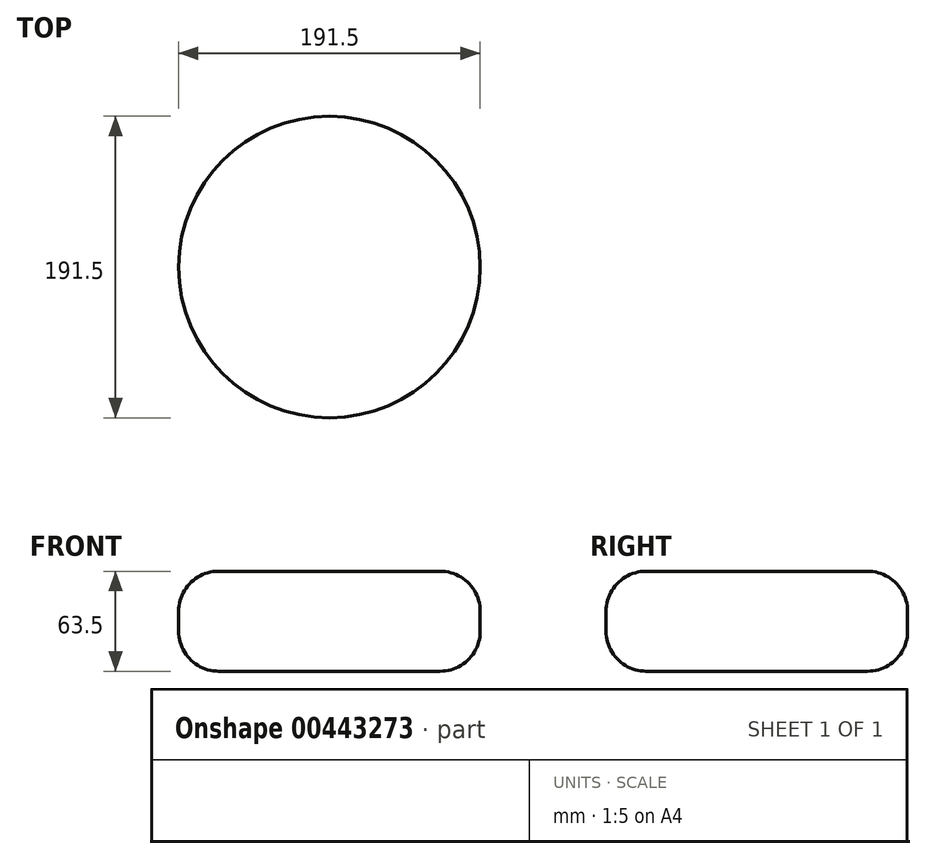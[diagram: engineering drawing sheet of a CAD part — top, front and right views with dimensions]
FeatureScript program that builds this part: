
annotation { "Feature Type Name" : "Feature", "Feature Type Description" : "" }
export const myFeature = defineFeature(function(context is Context, id is Id, definition is map)
    precondition{}
    {
        {
            var Q0;
            Q0=qCreatedBy(makeId("Top.planeOp"),FACE);
            var sketch = newSketch(context, id + "F0", { "sketchPlane" : qUnion([Q0])});
            skCircle(sketch, "E0", {"center": v(0, 0) * mm, "radius": 95.75 * mm});
            skSolve(sketch);
        }
        {
            var Q0;
            Q0=makeQuery(id+"F0.imprint","IMPRINT",FACE,{"disambiguationData":[TD([[makeQuery(id+"F0.imprint","IMPRINT",EDGE,{"derivedFrom":sQuery(id+"F0.wireOp",EDGE,"E0")}),1.0]])]});
            var Q1;
            Q1=sQuery(id+"F0.wireOp",EDGE,"E0");
            extrude(context, id + "F1", {"entities" : qUnion([Q0]), "surfaceEntities" : qUnion([Q1]), "depth" : 63.5 * mm});
        }
        {
            var Q0;
            Q0=makeQuery(id+"F1.opExtrude","CAP_FACE",FACE,{"disambiguationData":[OSD([sQuery(id+"F0.wireOp",EDGE,"E0")])],"isStart":false});
            var Q1;
            Q1=makeQuery(id+"F1.opExtrude","CAP_EDGE",EDGE,{"disambiguationData":[OSD([sQuery(id+"F0.wireOp",EDGE,"E0")])],"isStart":false});
            var Q2;
            Q2=makeQuery(id+"F1.opExtrude","SWEPT_FACE",FACE,{"disambiguationData":[OSD([sQuery(id+"F0.wireOp",EDGE,"E0")])]});
            fillet(context, id + "F2", {"entities" : qUnion([Q0, Q1, Q2]), "radius" : 25.4 * mm, "tangentPropagation" : true, "allowEdgeOverflow" : false});
        }
    });
